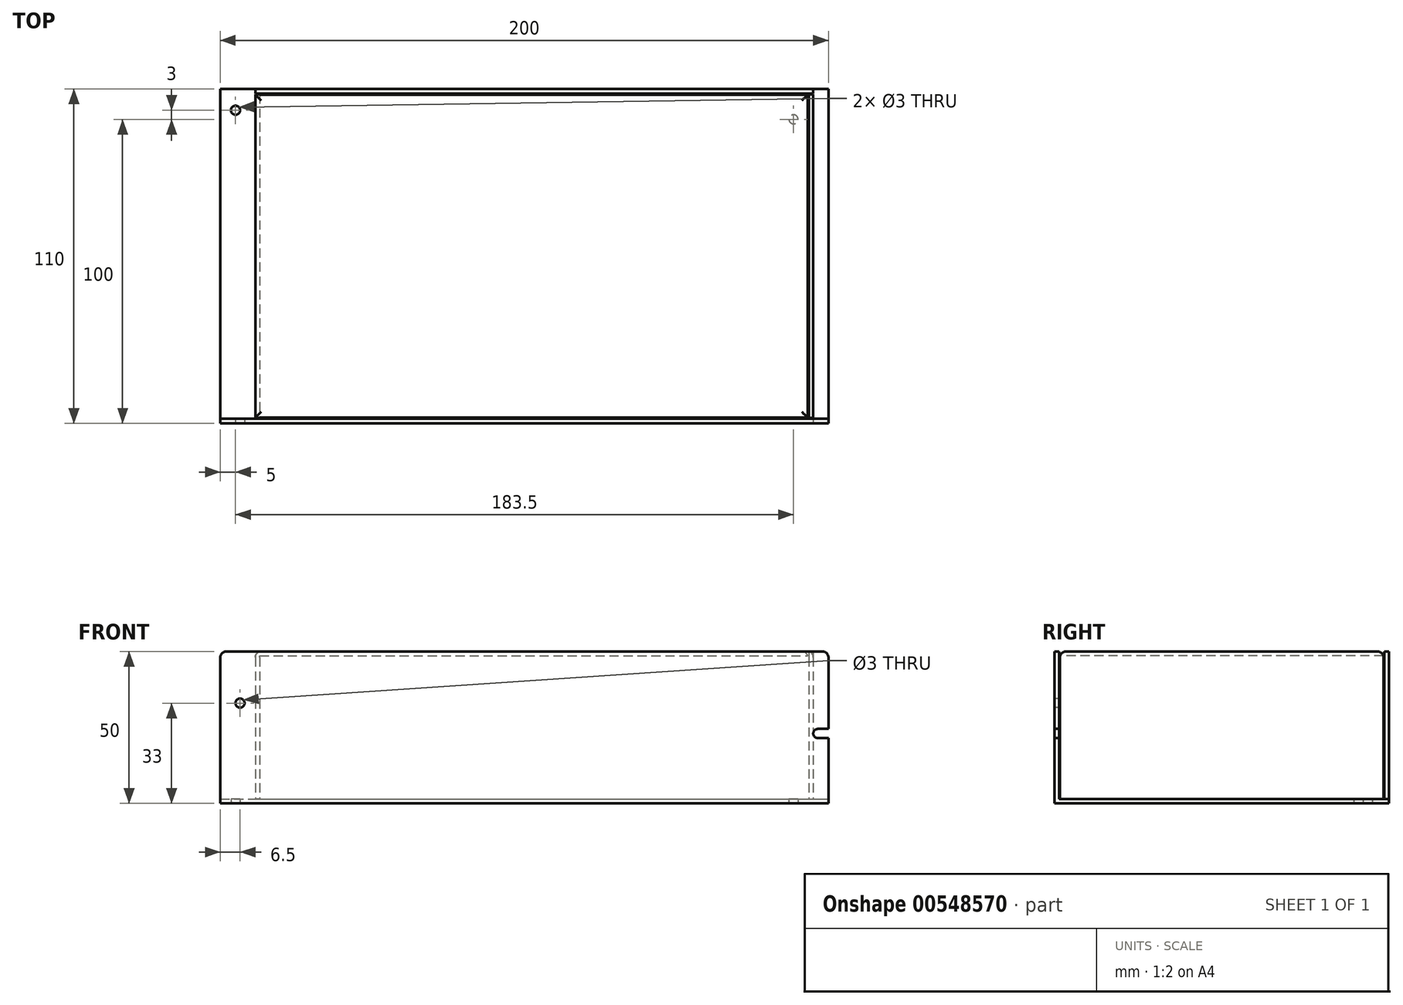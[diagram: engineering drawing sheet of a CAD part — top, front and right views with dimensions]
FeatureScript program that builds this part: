
annotation { "Feature Type Name" : "Feature", "Feature Type Description" : "" }
export const myFeature = defineFeature(function(context is Context, id is Id, definition is map)
    precondition{}
    {
        {
            var Q0;
            Q0=qCreatedBy(makeId("Top.planeOp"),FACE);
            var sketch = newSketch(context, id + "F0", { "sketchPlane" : qUnion([Q0])});
            skLineSegment(sketch, "E0.bottom", {"start": v(0, 0) * mm, "end": v(200, 0) * mm});
            skLineSegment(sketch, "E0.top", {"start": v(0, 110) * mm, "end": v(200, 110) * mm});
            skLineSegment(sketch, "E0.left", {"start": v(0, 0) * mm, "end": v(0, 110) * mm});
            skLineSegment(sketch, "E0.right", {"start": v(200, 0) * mm, "end": v(200, 110) * mm});
            skSolve(sketch);
        }
        {
            var Q0;
            Q0 = qSketchRegion(id + "F0", true);
            extrude(context, id + "F1", {"entities" : qUnion([Q0]), "depth" : 1.5 * mm, "offsetDistance" : 25 * mm});
        }
        {
            var Q0;
            Q0=makeQuery(id+"F1.opExtrude","CAP_FACE",FACE,{"disambiguationData":[OSD([sQuery(id+"F0.wireOp",EDGE,"E0.bottom"),sQuery(id+"F0.wireOp",EDGE,"E0.top"),sQuery(id+"F0.wireOp",EDGE,"E0.left"),sQuery(id+"F0.wireOp",EDGE,"E0.right")])],"isStart":false});
            var sketch = newSketch(context, id + "F2", { "sketchPlane" : qUnion([Q0])});
            skLineSegment(sketch, "E1.bottom", {"start": v(0, 0) * mm, "end": v(200, 0) * mm});
            skLineSegment(sketch, "E1.top", {"start": v(0, 1.5) * mm, "end": v(200, 1.5) * mm});
            skLineSegment(sketch, "E1.left", {"start": v(0, 0) * mm, "end": v(0, 1.5) * mm});
            skLineSegment(sketch, "E1.right", {"start": v(200, 0) * mm, "end": v(200, 1.5) * mm});
            skLineSegment(sketch, "E2.bottom", {"start": v(193.5, 1.5) * mm, "end": v(195, 1.5) * mm});
            skLineSegment(sketch, "E2.top", {"start": v(193.5, 110) * mm, "end": v(195, 110) * mm});
            skLineSegment(sketch, "E2.left", {"start": v(193.5, 1.8) * mm, "end": v(193.5, 108.2) * mm});
            skLineSegment(sketch, "E2.right", {"start": v(195, 1.8) * mm, "end": v(195, 108.2) * mm});
            skLineSegment(sketch, "E3.bottom", {"start": v(193.5, 110) * mm, "end": v(11.5, 110) * mm});
            skLineSegment(sketch, "E3.top", {"start": v(193.5, 108.5) * mm, "end": v(11.5, 108.5) * mm});
            skLineSegment(sketch, "E3.left", {"start": v(193.5, 110) * mm, "end": v(193.5, 108.5) * mm});
            skLineSegment(sketch, "E3.right", {"start": v(11.5, 110) * mm, "end": v(11.5, 108.5) * mm});
            skLineSegment(sketch, "E4.bottom", {"start": v(11.5, 108.5) * mm, "end": v(13, 108.5) * mm});
            skLineSegment(sketch, "E4.top", {"start": v(11.5, 1.5) * mm, "end": v(13, 1.5) * mm});
            skLineSegment(sketch, "E4.left", {"start": v(11.5, 108.2) * mm, "end": v(11.5, 1.8) * mm});
            skLineSegment(sketch, "E4.right", {"start": v(13, 108.2) * mm, "end": v(13, 1.8) * mm});
            skLineSegment(sketch, "E5", {"start": v(193.5, 1.8) * mm, "end": v(195, 1.8) * mm});
            skLineSegment(sketch, "E6", {"start": v(193.5, 108.5) * mm, "end": v(195, 108.5) * mm});
            skLineSegment(sketch, "E7", {"start": v(195, 108.2) * mm, "end": v(193.5, 108.2) * mm});
            skLineSegment(sketch, "E8", {"start": v(13, 1.8) * mm, "end": v(11.5, 1.8) * mm});
            skLineSegment(sketch, "E9", {"start": v(11.5, 108.2) * mm, "end": v(13, 108.2) * mm});
            skLineSegment(sketch, "E10.trimOffspring", {"start": v(195, 108.5) * mm, "end": v(195, 110) * mm});
            skLineSegment(sketch, "E11.trimOffspring", {"start": v(193.5, 108.5) * mm, "end": v(193.5, 110) * mm});
            skSolve(sketch);
        }
        {
            var Q0;
            Q0 = qSketchRegion(id + "F2", true);
            extrude(context, id + "F3", {"entities" : qUnion([Q0]), "operationType" : NewBodyOperationType.ADD, "depth" : (50 - 1.5) * mm, "offsetDistance" : 25 * mm});
        }
        {
            var Q0;
            Q0=makeQuery(id+"F3.opExtrude","CAP_FACE",FACE,{"disambiguationData":[OSD([sQuery(id+"F2.wireOp",EDGE,"E1.bottom"),sQuery(id+"F2.wireOp",EDGE,"E1.top"),sQuery(id+"F2.wireOp",EDGE,"E1.left"),sQuery(id+"F2.wireOp",EDGE,"E1.right"),sQuery(id+"F2.wireOp",EDGE,"E2.top"),sQuery(id+"F2.wireOp",EDGE,"E2.left"),sQuery(id+"F2.wireOp",EDGE,"E2.right"),sQuery(id+"F2.wireOp",EDGE,"E3.bottom"),sQuery(id+"F2.wireOp",EDGE,"E3.top"),sQuery(id+"F2.wireOp",EDGE,"E3.right"),sQuery(id+"F2.wireOp",EDGE,"E4.left"),sQuery(id+"F2.wireOp",EDGE,"E4.right")])],"isStart":false});
            var sketch = newSketch(context, id + "F4", { "sketchPlane" : qUnion([Q0])});
            skLineSegment(sketch, "E12.bottom", {"start": v(13, 108.2) * mm, "end": v(193.2, 108.2) * mm});
            skLineSegment(sketch, "E12.top", {"start": v(13, 1.8) * mm, "end": v(193.2, 1.8) * mm});
            skLineSegment(sketch, "E12.left", {"start": v(13, 108.2) * mm, "end": v(13, 1.8) * mm});
            skLineSegment(sketch, "E12.right", {"start": v(193.2, 108.2) * mm, "end": v(193.2, 1.8) * mm});
            skSolve(sketch);
        }
        {
            var Q0;
            Q0 = qSketchRegion(id + "F4", true);
            extrude(context, id + "F5", {"entities" : qUnion([Q0]), "operationType" : NewBodyOperationType.ADD, "oppositeDirection" : true, "depth" : 1.5 * mm, "offsetDistance" : 25 * mm});
        }
        {
            var Q0;
            Q0=makeQuery(id+"F3.boolean.opBoolean","MERGE",FACE,{"derivedFrom":[makeQuery(id+"F1.opExtrude","SWEPT_FACE",FACE,{"disambiguationData":[OSD([sQuery(id+"F0.wireOp",EDGE,"E0.bottom")])]}),makeQuery(id+"F3.opExtrude","SWEPT_FACE",FACE,{"disambiguationData":[OSD([sQuery(id+"F2.wireOp",EDGE,"E1.bottom")])]})]});
            var sketch = newSketch(context, id + "F6", { "sketchPlane" : qUnion([Q0])});
            skCircle(sketch, "E13", {"center": v(196.5, 23) * mm, "radius": 1.5 * mm});
            skLineSegment(sketch, "E14.bottom", {"start": v(196.5, 24.5) * mm, "end": v(200, 24.5) * mm});
            skLineSegment(sketch, "E14.top", {"start": v(196.5, 21.5) * mm, "end": v(200, 21.5) * mm});
            skLineSegment(sketch, "E14.left", {"start": v(196.5, 24.5) * mm, "end": v(196.5, 21.5) * mm});
            skLineSegment(sketch, "E14.right", {"start": v(200, 24.5) * mm, "end": v(200, 21.5) * mm});
            skCircle(sketch, "E15", {"center": v(6.5, 33) * mm, "radius": 1.5 * mm});
            skSolve(sketch);
        }
        {
            var Q0;
            Q0 = qSketchRegion(id + "F6", true);
            extrude(context, id + "F7", {"entities" : qUnion([Q0]), "operationType" : NewBodyOperationType.REMOVE, "oppositeDirection" : true, "depth" : 2 * mm, "offsetDistance" : 25 * mm});
        }
        {
            var Q0;
            Q0=makeQuery(id+"F3.opExtrude","CAP_EDGE",EDGE,{"disambiguationData":[OSD([sQuery(id+"F2.wireOp",EDGE,"E1.right")])],"isStart":false});
            var Q1;
            Q1=makeQuery(id+"F3.opExtrude","CAP_EDGE",EDGE,{"disambiguationData":[OSD([sQuery(id+"F2.wireOp",EDGE,"E5")])],"isStart":false});
            var Q2;
            Q2=makeQuery(id+"F3.opExtrude","CAP_EDGE",EDGE,{"disambiguationData":[OSD([sQuery(id+"F2.wireOp",EDGE,"E1.left")])],"isStart":false});
            var Q3;
            Q3=makeQuery(id+"F3.opExtrude","CAP_EDGE",EDGE,{"disambiguationData":[OSD([sQuery(id+"F2.wireOp",EDGE,"E8")])],"isStart":false});
            var Q4;
            Q4=makeQuery(id+"F3.opExtrude","CAP_EDGE",EDGE,{"disambiguationData":[OSD([sQuery(id+"F2.wireOp",EDGE,"E9")])],"isStart":false});
            var Q5;
            Q5=makeQuery(id+"F3.opExtrude","CAP_EDGE",EDGE,{"disambiguationData":[OSD([sQuery(id+"F2.wireOp",EDGE,"E3.right")])],"isStart":false});
            var Q6;
            Q6=makeQuery(id+"F3.opExtrude","CAP_EDGE",EDGE,{"disambiguationData":[OSD([sQuery(id+"F2.wireOp",EDGE,"E7")])],"isStart":false});
            var Q7;
            Q7=makeQuery(id+"F3.opExtrude","CAP_EDGE",EDGE,{"disambiguationData":[OSD([sQuery(id+"F2.wireOp",EDGE,"E10.trimOffspring")])],"isStart":false});
            var Q8;
            Q8=makeQuery(id+"F5.opExtrude","CAP_EDGE",EDGE,{"disambiguationData":[OSD([sQuery(id+"F4.wireOp",EDGE,"E12.right")])],"isStart":true});
            var Q9;
            Q9=makeQuery(id+"F3.opExtrude","CAP_EDGE",EDGE,{"disambiguationData":[OSD([sQuery(id+"F2.wireOp",EDGE,"E4.left")])],"isStart":false});
            fillet(context, id + "F8", {"entities" : qUnion([Q0, Q1, Q2, Q3, Q4, Q5, Q6, Q7, Q8, Q9]), "radius" : 2 * mm, "tangentPropagation" : true, "allowEdgeOverflow" : false});
        }
        {
            var Q0;
            Q0=makeQuery(id+"F1.opExtrude","CAP_FACE",FACE,{"disambiguationData":[OSD([sQuery(id+"F0.wireOp",EDGE,"E0.bottom"),sQuery(id+"F0.wireOp",EDGE,"E0.top"),sQuery(id+"F0.wireOp",EDGE,"E0.left"),sQuery(id+"F0.wireOp",EDGE,"E0.right")])],"isStart":true});
            var sketch = newSketch(context, id + "F9", { "sketchPlane" : qUnion([Q0])});
            skCircle(sketch, "E16", {"center": v(188.5, -100) * mm, "radius": 1.5 * mm});
            skCircle(sketch, "E17", {"center": v(5, -103) * mm, "radius": 1.5 * mm});
            skSolve(sketch);
        }
        {
            var Q0;
            Q0 = qSketchRegion(id + "F9", true);
            extrude(context, id + "F10", {"entities" : qUnion([Q0]), "operationType" : NewBodyOperationType.REMOVE, "oppositeDirection" : true, "depth" : 25 * mm, "offsetDistance" : 25 * mm});
        }
    });
